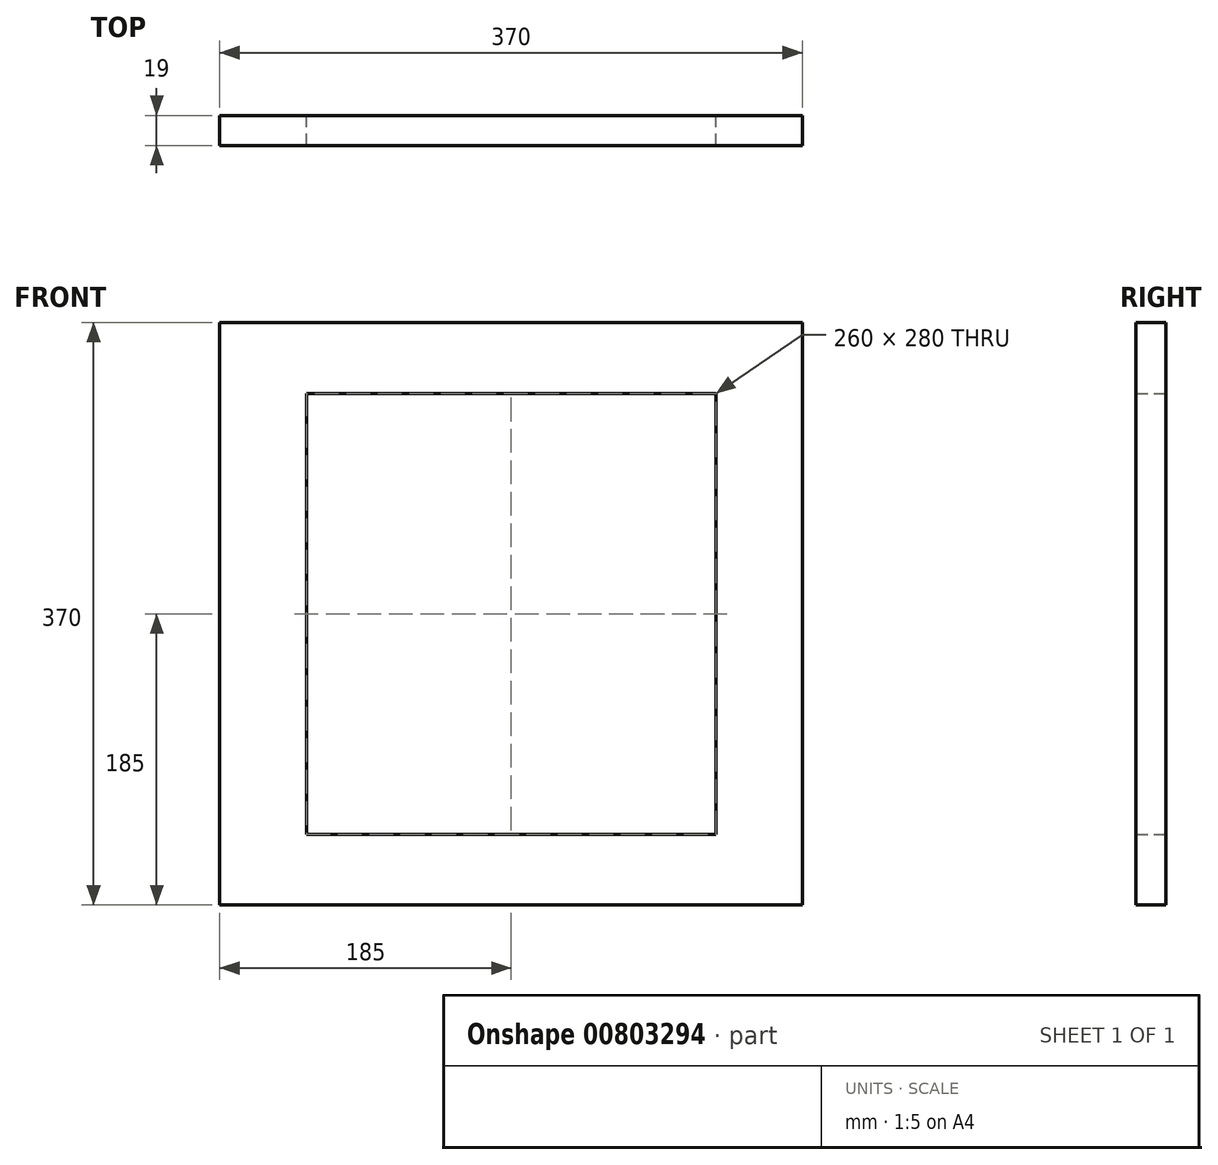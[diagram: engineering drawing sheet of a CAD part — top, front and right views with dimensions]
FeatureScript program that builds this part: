
annotation { "Feature Type Name" : "Feature", "Feature Type Description" : "" }
export const myFeature = defineFeature(function(context is Context, id is Id, definition is map)
    precondition{}
    {
        {
            var Q0;
            Q0=qCreatedBy(makeId("Front.planeOp"),FACE);
            var sketch = newSketch(context, id + "F0", { "sketchPlane" : qUnion([Q0])});
            skLineSegment(sketch, "E0.bottom", {"start": v(185, -185) * mm, "end": v(-185, -185) * mm});
            skLineSegment(sketch, "E0.top", {"start": v(185, 185) * mm, "end": v(-185, 185) * mm});
            skLineSegment(sketch, "E0.left", {"start": v(185, -185) * mm, "end": v(185, 185) * mm});
            skLineSegment(sketch, "E0.right", {"start": v(-185, -185) * mm, "end": v(-185, 185) * mm});
            skPoint(sketch, "E0.middle", {"position": v(0, 0) * mm});
            skLineSegment(sketch, "E1.bottom", {"start": v(130, -140) * mm, "end": v(-130, -140) * mm});
            skLineSegment(sketch, "E1.top", {"start": v(130, 140) * mm, "end": v(-130, 140) * mm});
            skLineSegment(sketch, "E1.left", {"start": v(130, -140) * mm, "end": v(130, 140) * mm});
            skLineSegment(sketch, "E1.right", {"start": v(-130, -140) * mm, "end": v(-130, 140) * mm});
            skSolve(sketch);
        }
        {
            var Q0;
            Q0=makeQuery(id+"F0.imprint","IMPRINT",FACE,{"disambiguationData":[TD([[makeQuery(id+"F0.imprint","IMPRINT",EDGE,{"derivedFrom":sQuery(id+"F0.wireOp",EDGE,"E0.bottom")}),-1.0]])]});
            extrude(context, id + "F1", {"entities" : qUnion([Q0]), "depth" : 19 * mm, "offsetDistance" : 25 * mm});
        }
    });
